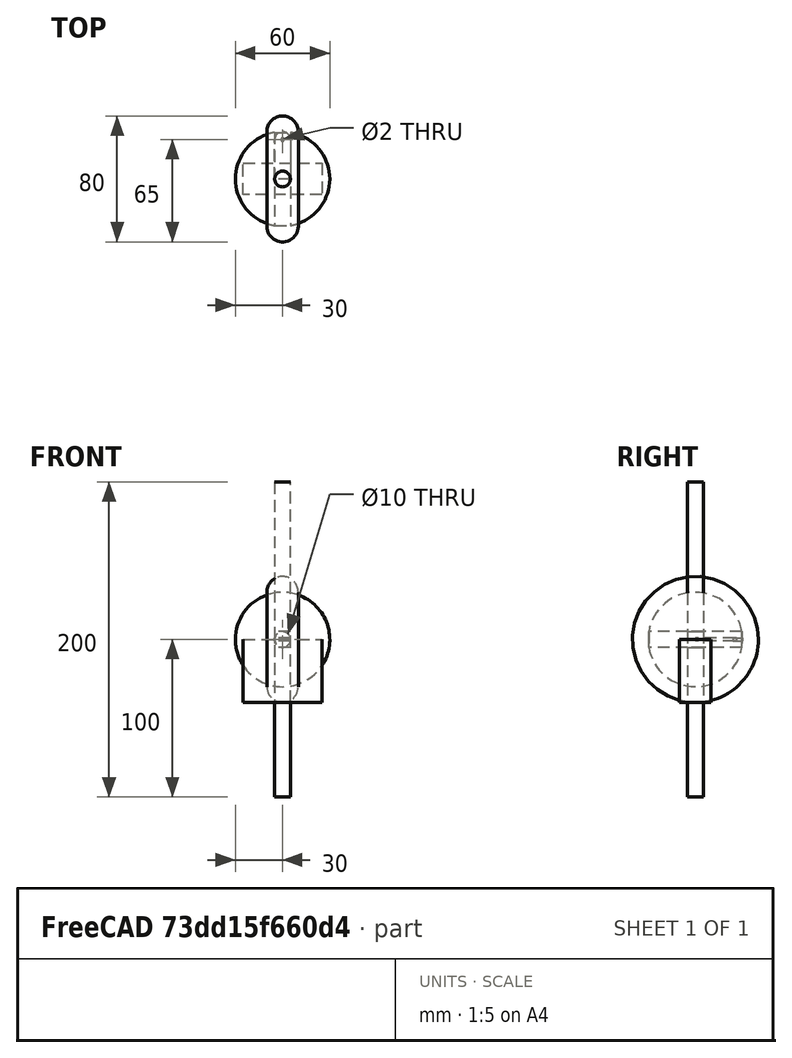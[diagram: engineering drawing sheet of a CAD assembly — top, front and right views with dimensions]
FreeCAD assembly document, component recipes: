
FREECAD ASSEMBLY — COMPONENT RECIPES ("NikraDAPBeginnersTutorial2")

This assembly document has 7 components, labeled P0..P6 below (a component is one placed body or linked part). 6 of them carry a construction recipe — the FreeCAD feature program that regenerates the part from scratch, quoted from this document or its linked companion documents; the rest are supplied as boundary geometry only. No exploded tour is included for this assembly.
COMPONENT P0 — recipe-attached ("LugBody", modeled in this document).
Construction recipe (the document's own serialized feature program — sketch geometry with constraints, then the solid features built on it; lengths are millimeters unless a unit is written):

FEATURE [Sketcher::SketchObject] Sketch
  FullyConstrained = true
  MapMode = 5
  Support = -> [XY_Plane]
  sketch-geometry (5):
    g0: LineSegment StartX=-5 StartY=0 StartZ=0 EndX=-5 EndY=25 EndZ=0
    g1: LineSegment StartX=5 StartY=25 StartZ=0 EndX=5 EndY=0 EndZ=0
    g2: LineSegment StartX=5 StartY=0 StartZ=0 EndX=-5 EndY=0 EndZ=0
    g3: Circle CenterX=0 CenterY=25 CenterZ=0 NormalX=0 NormalY=0 NormalZ=1 AngleXU=0 Radius=1
    g4: ArcOfCircle CenterX=0 CenterY=25 CenterZ=0 NormalX=0 NormalY=0 NormalZ=1 AngleXU=0 Radius=5 StartAngle=5e-16 EndAngle=3.1416
  constraints (13):
    c: PointOnObject(g0,g-1)
    c: Vertical(g0)
    c: Coincident(g1,g2)
    c: Coincident(g2,g0)
    c: Vertical(g1)
    c: Symmetric(g0,g1,g-1)
    c: Radius(g3) = 1
    c: Distance(g1) = 25
    c: Coincident(g4,g3)
    c: Coincident(g4,g0)
    c: Radius(g4) = 5
    c: Tangent(g4,g1) = 1.5708
    c: PointOnObject(g3,g-2)
FEATURE [PartDesign::Pad] Pad004
  Direction = (0,0,1)
  Length = 2
  Length2 = 10
  Midplane = true
  Profile = -> Sketch
  ReferenceAxis = -> Sketch [N_Axis]
  Type = 0
FEATURE [PartDesign::CoordinateSystem] LugFace
  AttacherType = Attacher::AttachEngine3D
  MapMode = 5
  Placement = pos=(0,0,0) rot=(1,0,0;1.5708rad)
  Support = -> [Pad004]
FEATURE [PartDesign::CoordinateSystem] LugHole
  AttacherType = Attacher::AttachEngine3D
  MapMode = 11
  Placement = pos=(0,25,1) rot=(0,0,1;1.5708rad)
  Support = -> [Pad004]
FEATURE [PartDesign::CoordinateSystem] LugHoleRot
  AttacherType = Attacher::AttachEngine3D
  AttachmentOffset = pos=(0,0,0) rot=(0,0,1;0.523599rad)
  MapMode = 11
  Placement = pos=(0,25,1) rot=(0,0,1;2.0944rad)
  Support = -> [Pad004]
FEATURE [PartDesign::Body] Body  label="LugBody"
  Group = -> [Sketch,Pad004,LugFace,LugHole,LugHoleRot]
  Origin = -> Origin
  Tip = -> Pad004
COMPONENT P1 — recipe-attached ("RodBody", modeled in this document).
Construction recipe (the document's own serialized feature program — sketch geometry with constraints, then the solid features built on it; lengths are millimeters unless a unit is written):

FEATURE [Sketcher::SketchObject] Sketch001
  FullyConstrained = true
  MapMode = 5
  Support = -> [XY_Plane001]
  sketch-geometry (1):
    g0: Circle CenterX=0 CenterY=0 CenterZ=0 NormalX=0 NormalY=0 NormalZ=1 AngleXU=0 Radius=5
  constraints (2):
    c: Coincident(g0,g-1)
    c: Radius(g0) = 5
FEATURE [PartDesign::Pad] Pad
  Direction = (0,0,1)
  Length = 200
  Length2 = 10
  Midplane = true
  Profile = -> Sketch001
  ReferenceAxis = -> Sketch001 [N_Axis]
  Type = 0
FEATURE [PartDesign::CoordinateSystem] RodTop
  AttacherType = Attacher::AttachEngine3D
  MapMode = 11
  Placement = pos=(0,0,100) rot=(0,0,1;1.5708rad)
  Support = -> [Pad]
FEATURE [PartDesign::CoordinateSystem] RodBot
  AttacherType = Attacher::AttachEngine3D
  MapMode = 11
  Placement = pos=(0,0,-100) rot=(0,0,1;1.5708rad)
  Support = -> [Pad]
FEATURE [PartDesign::Body] Body001  label="RodBody"
  Group = -> [Sketch001,Pad,RodTop,RodBot]
  Origin = -> Origin001
  Tip = -> Pad
COMPONENT P2 — recipe-attached ("BobBody", modeled in this document).
Construction recipe (the document's own serialized feature program — sketch geometry with constraints, then the solid features built on it; lengths are millimeters unless a unit is written):

FEATURE [Sketcher::SketchObject] Sketch004
  FullyConstrained = true
  MapMode = 5
  Support = -> [XY_Plane004]
  sketch-geometry (4):
    g0: LineSegment StartX=-10 StartY=0 StartZ=0 EndX=-10 EndY=30 EndZ=0
    g1: ArcOfCircle CenterX=0 CenterY=30 CenterZ=0 NormalX=0 NormalY=0 NormalZ=1 AngleXU=0 Radius=10 StartAngle=2e-16 EndAngle=3.14159
    g2: LineSegment StartX=10 StartY=30 StartZ=0 EndX=10 EndY=0 EndZ=0
    g3: LineSegment StartX=10 StartY=0 StartZ=0 EndX=-10 EndY=0 EndZ=0
  constraints (11):
    c: PointOnObject(g0,g-1)
    c: Vertical(g0)
    c: Tangent(g0,g1) = 1.5708
    c: Tangent(g1,g2) = 1.5708
    c: Coincident(g2,g3)
    c: Coincident(g3,g0)
    c: Vertical(g2)
    c: PointOnObject(g1,g-2)
    c: Diameter(g1) = 20
    c: Distance(g0) = 30
    c: PointOnObject(g2,g-1)
FEATURE [PartDesign::Revolution] Revolution001
  Angle = 360
  Axis = (1,0,0)
  Base = (0,0,0)
  Profile = -> Sketch004
  ReferenceAxis = -> Sketch004 [H_Axis]
FEATURE [PartDesign::CoordinateSystem] BobSurface
  AttacherType = Attacher::AttachEngine3D
  MapMode = 11
  Placement = pos=(10,-3.6e-15,0) rot=(0.707107,0,0.707107;3.14159rad)
  Support = -> [Revolution001]
FEATURE [PartDesign::Body] Body004  label="BobBody"
  Group = -> [Sketch004,Revolution001,BobSurface]
  Origin = -> Origin004
  Tip = -> Revolution001
COMPONENT P3 — recipe-attached ("GroundBody", modeled in this document).
Construction recipe (the document's own serialized feature program — sketch geometry with constraints, then the solid features built on it; lengths are millimeters unless a unit is written):

FEATURE [Sketcher::SketchObject] Sketch005
  FullyConstrained = true
  MapMode = 5
  Support = -> [XY_Plane005]
  sketch-geometry (4):
    g0: LineSegment StartX=-25 StartY=10 StartZ=0 EndX=25 EndY=10 EndZ=0
    g1: LineSegment StartX=25 StartY=10 StartZ=0 EndX=25 EndY=-10 EndZ=0
    g2: LineSegment StartX=25 StartY=-10 StartZ=0 EndX=-25 EndY=-10 EndZ=0
    g3: LineSegment StartX=-25 StartY=-10 StartZ=0 EndX=-25 EndY=10 EndZ=0
  constraints (11):
    c: Coincident(g0,g1)
    c: Coincident(g1,g2)
    c: Coincident(g2,g3)
    c: Coincident(g3,g0)
    c: Horizontal(g0)
    c: Horizontal(g2)
    c: Vertical(g1)
    c: Vertical(g3)
    c: DistanceY(g2,g0) = 20
    c: DistanceX(g0,g0) = 50
    c: Symmetric(g0,g1,g-1)
FEATURE [PartDesign::Pad] Pad003
  Direction = (0,0,1)
  Length = 40
  Length2 = 10
  Profile = -> Sketch005
  ReferenceAxis = -> Sketch005 [N_Axis]
  Reversed = true
  Type = 0
FEATURE [PartDesign::CoordinateSystem] GroundFace
  AttacherType = Attacher::AttachEngine3D
  MapMode = 5
  Support = -> [Pad003]
FEATURE [PartDesign::Body] Body005  label="GroundBody"
  Group = -> [Sketch005,Pad003,GroundFace]
  Origin = -> Origin005
  Tip = -> Pad003
COMPONENT P4 — recipe-attached ("ShortRodBody", modeled in this document).
Construction recipe (the document's own serialized feature program — sketch geometry with constraints, then the solid features built on it; lengths are millimeters unless a unit is written):

FEATURE [Sketcher::SketchObject] Sketch006
  FullyConstrained = true
  MapMode = 5
  Support = -> [XY_Plane007]
  sketch-geometry (1):
    g0: Circle CenterX=0 CenterY=0 CenterZ=0 NormalX=0 NormalY=0 NormalZ=1 AngleXU=0 Radius=5
  constraints (2):
    c: Coincident(g0,g-1)
    c: Radius(g0) = 5
FEATURE [PartDesign::Pad] Pad005
  Direction = (0,0,1)
  Length = 10
  Length2 = 10
  Midplane = true
  Profile = -> Sketch006
  ReferenceAxis = -> Sketch006 [N_Axis]
  Type = 0
FEATURE [PartDesign::CoordinateSystem] MiniRodTop
  AttacherType = Attacher::AttachEngine3D
  MapMode = 11
  Placement = pos=(0,0,5) rot=(0,0,1;1.5708rad)
  Support = -> [Pad005]
FEATURE [PartDesign::CoordinateSystem] MiniRodBot
  AttacherType = Attacher::AttachEngine3D
  MapMode = 11
  Placement = pos=(0,0,-5) rot=(0,0,1;1.5708rad)
  Support = -> [Pad005]
FEATURE [PartDesign::Body] Body006  label="ShortRodBody"
  Group = -> [Sketch006,Pad005,MiniRodTop,MiniRodBot]
  Origin = -> Origin007
  Tip = -> Pad005
COMPONENT P5 — recipe-attached ("Weight", modeled in this document).
Construction recipe (the document's own serialized feature program — sketch geometry with constraints, then the solid features built on it; lengths are millimeters unless a unit is written):

FEATURE [Sketcher::SketchObject] Sketch007
  FullyConstrained = true
  MapMode = 5
  Support = -> [XY_Plane009]
  sketch-geometry (2):
    g0: ArcOfCircle CenterX=0 CenterY=0 CenterZ=0 NormalX=0 NormalY=0 NormalZ=1 AngleXU=0 Radius=30 StartAngle=1.73824 EndAngle=4.54494
    g1: LineSegment StartX=-5 StartY=29.5804 StartZ=0 EndX=-5 EndY=-29.5804 EndZ=0
  constraints (6):
    c: Vertical(g1)
    c: Coincident(g0,g1)
    c: Coincident(g0,g1)
    c: Radius(g0) = 30
    c: Coincident(g0,g-1)
    c: DistanceX(g0,g0) = 5
FEATURE [PartDesign::Revolution] Revolution
  Angle = 360
  Axis = (0,1,0)
  Base = (0,0,0)
  Profile = -> Sketch007
  ReferenceAxis = -> Sketch007 [V_Axis]
FEATURE [PartDesign::CoordinateSystem] WeightOrigin
  AttacherType = Attacher::AttachEngine3D
  AttachmentOffset = pos=(0,0,30) rot=(0,0,1;0rad)
  MapMode = 11
  Placement = pos=(0,0.419601,0) rot=(0.57735,0.57735,0.57735;4.18879rad)
  Support = -> [Revolution]
FEATURE [PartDesign::Body] Body007  label="Weight"
  Group = -> [Sketch007,Revolution,WeightOrigin]
  Origin = -> Origin009
  Tip = -> Revolution
COMPONENT P6 — geometry summary ("Model"; no construction recipe available for this part):
  bounding box: 290.2 x 167.7 x 60.0 mm
  tessellated surface: 9,208 triangles
  volume: 165270 mm^3 (6% of its bounding box)
PROVENANCE & LICENSES
A FreeCAD (.FCStd) document from a public repository crawl; recipes are the document's own serialized feature recipes (and, for linked parts, companion documents' recipes).
License: gpl-3.0.
